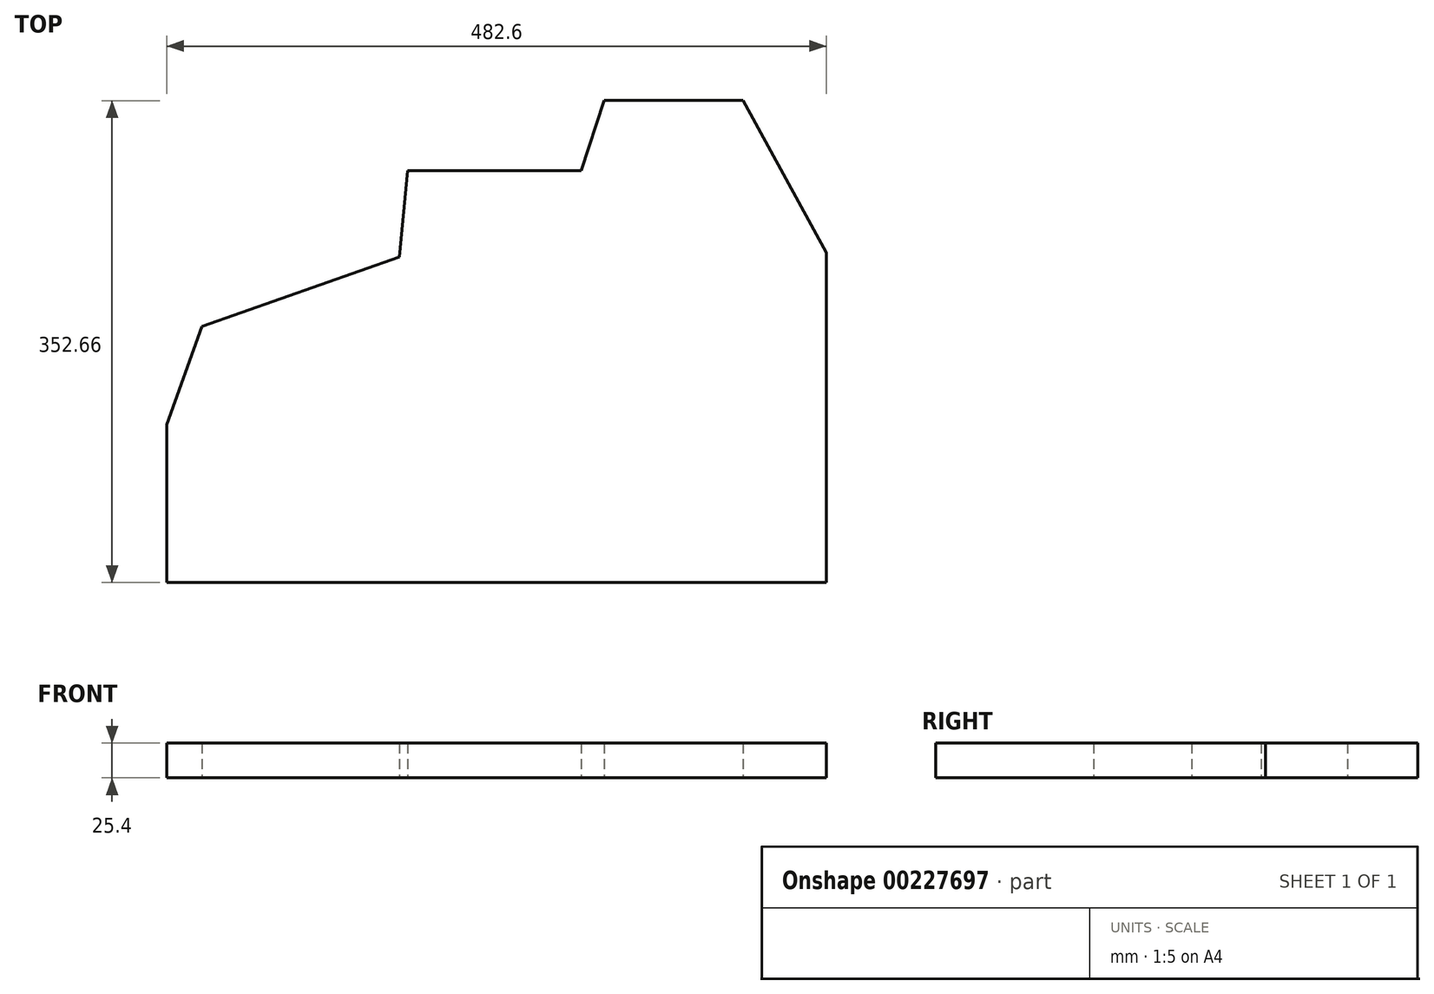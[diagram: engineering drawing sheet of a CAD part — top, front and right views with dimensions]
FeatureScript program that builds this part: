
annotation { "Feature Type Name" : "Feature", "Feature Type Description" : "" }
export const myFeature = defineFeature(function(context is Context, id is Id, definition is map)
    precondition{}
    {
        {
            var Q0;
            Q0=qCreatedBy(makeId("Top.planeOp"),FACE);
            var sketch = newSketch(context, id + "F0", { "sketchPlane" : qUnion([Q0])});
            skLineSegment(sketch, "E0", {"start": v(383.09, -115.53) * mm, "end": v(-99.51, -115.53) * mm});
            skLineSegment(sketch, "E1", {"start": v(-99.51, -115.53) * mm, "end": v(-99.51, 0) * mm});
            skLineSegment(sketch, "E2", {"start": v(70.76, 122.53) * mm, "end": v(76.6, 185.76) * mm});
            skLineSegment(sketch, "E3", {"start": v(76.6, 185.76) * mm, "end": v(203.6, 185.76) * mm});
            skLineSegment(sketch, "E4", {"start": v(203.6, 185.76) * mm, "end": v(220.42, 237.13) * mm});
            skLineSegment(sketch, "E5", {"start": v(220.42, 237.13) * mm, "end": v(322.02, 237.13) * mm});
            skLineSegment(sketch, "E6", {"start": v(383.09, -115.53) * mm, "end": v(383.09, 125.77) * mm});
            skLineSegment(sketch, "E7", {"start": v(322.02, 237.13) * mm, "end": v(383.09, 125.77) * mm});
            skLineSegment(sketch, "E8", {"start": v(70.76, 122.53) * mm, "end": v(-73.8, 71.73) * mm});
            skLineSegment(sketch, "E9", {"start": v(-73.8, 71.73) * mm, "end": v(-99.51, 0) * mm});
            skSolve(sketch);
        }
        {
            var Q0;
            Q0 = qSketchRegion(id + "F0", true);
            extrude(context, id + "F1", {"entities" : qUnion([Q0]), "depth" : 25.4 * mm});
        }
    });
